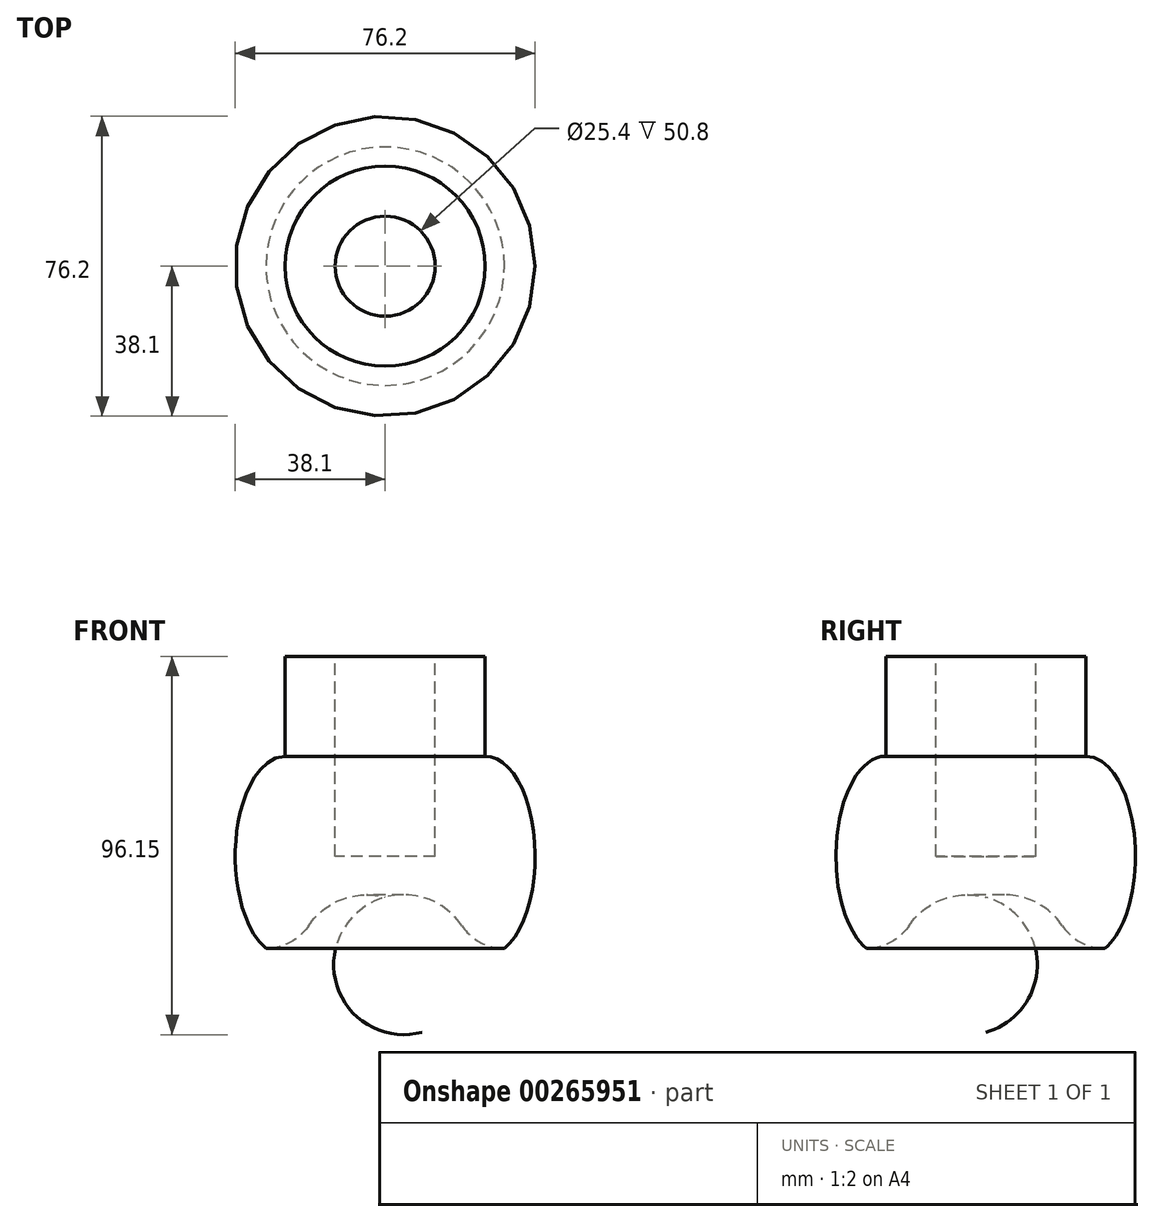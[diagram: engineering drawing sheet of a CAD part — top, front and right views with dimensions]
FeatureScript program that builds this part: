
annotation { "Feature Type Name" : "Feature", "Feature Type Description" : "" }
export const myFeature = defineFeature(function(context is Context, id is Id, definition is map)
    precondition{}
    {
        {
            var Q0;
            Q0=qCreatedBy(makeId("Front.planeOp"),FACE);
            var sketch = newSketch(context, id + "F0", { "sketchPlane" : qUnion([Q0])});
            skLineSegment(sketch, "E0", {"start": v(0, 0) * mm, "end": v(12.7, 0) * mm});
            skLineSegment(sketch, "E1", {"start": v(12.7, 0) * mm, "end": v(12.7, 50.8) * mm});
            skLineSegment(sketch, "E2", {"start": v(12.7, 50.8) * mm, "end": v(25.4, 50.8) * mm});
            skLineSegment(sketch, "E3", {"start": v(25.4, 50.8) * mm, "end": v(25.4, 25.4) * mm});
            skEllipticalArc(sketch, "E4", {});
            skPoint(sketch, "E5", {"position": v(25.4, 25.4) * mm});
            skPoint(sketch, "E6", {"position": v(12.7, 0) * mm});
            skPoint(sketch, "E7", {"position": v(38.1, 0) * mm});
            skPoint(sketch, "E8", {"position": v(25.27, -25.4) * mm});
            skArc(sketch, "E9", {"start": v(30.28, -23.45) * mm, "mid": v(24.15, -21.91) * mm, "end": v(19.46, -17.67) * mm});
            skLineSegment(sketch, "E10", {"start": v(0, 0) * mm, "end": v(0, -10.42) * mm});
            skLineSegment(sketch, "E11", {"start": v(0, -10.42) * mm, "end": v(0, -10.42) * mm});
            skArc(sketch, "E12.filletArc", {"start": v(19.46, -17.67) * mm, "mid": v(10.9, -10.91) * mm, "end": v(0, -10.42) * mm});
            const initialGuessF0  = {"E4": [0.0254, 0, 0, 1, 0.02540000155568123, 0.0127, 3.5362172818497446, 0]};
            skSetInitialGuess(sketch, initialGuessF0);
            skSolve(sketch);
        }
        {
            var Q0;
            Q0=makeQuery(id+"F0.imprint","IMPRINT",FACE,{"disambiguationData":[TD([[makeQuery(id+"F0.imprint","IMPRINT",EDGE,{"derivedFrom":sQuery(id+"F0.wireOp",EDGE,"E0")}),-1.0]])]});
            var Q1;
            Q1=sQuery(id+"F0.wireOp",EDGE,"E10");
            revolve(context, id + "F1", {"entities" : qUnion([Q0]), "axis" : qUnion([Q1]), "revolveType" : RevolveType.FULL});
        }
    });
